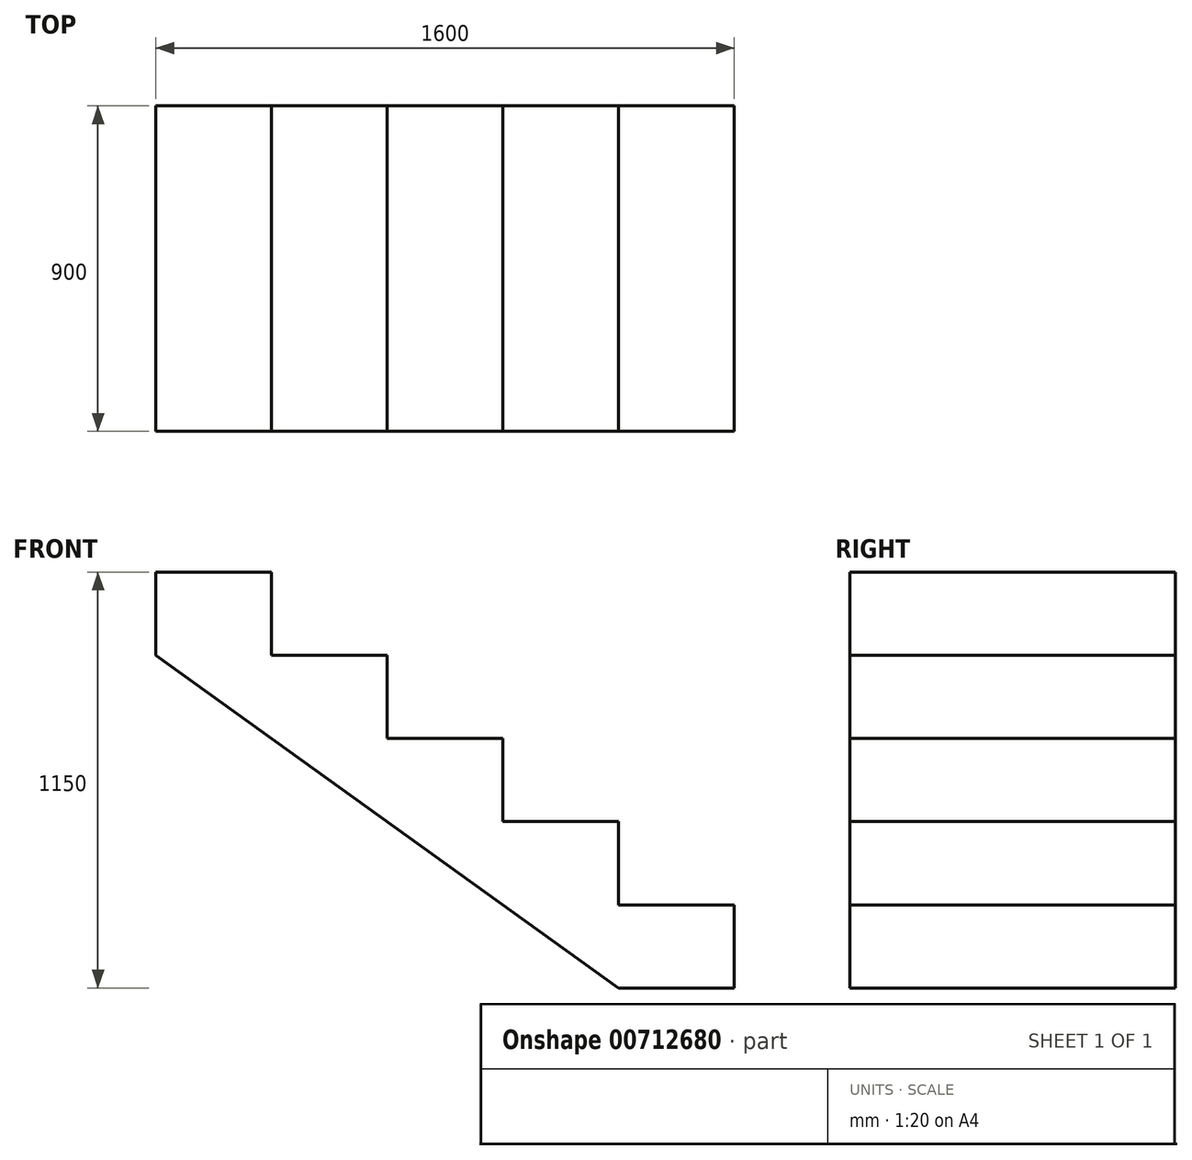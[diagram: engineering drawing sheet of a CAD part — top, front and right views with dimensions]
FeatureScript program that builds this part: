
annotation { "Feature Type Name" : "Feature", "Feature Type Description" : "" }
export const myFeature = defineFeature(function(context is Context, id is Id, definition is map)
    precondition{}
    {
        {
            var Q0;
            Q0=qCreatedBy(makeId("Front.planeOp"),FACE);
            var sketch = newSketch(context, id + "F0", { "sketchPlane" : qUnion([Q0])});
            skLineSegment(sketch, "E0", {"start": v(0, 0) * mm, "end": v(0, 230) * mm});
            skLineSegment(sketch, "E1", {"start": v(0, 230) * mm, "end": v(-320, 230) * mm});
            skLineSegment(sketch, "E2", {"start": v(-320, 230) * mm, "end": v(-320, 460) * mm});
            skLineSegment(sketch, "E3", {"start": v(-320, 460) * mm, "end": v(-640, 460) * mm});
            skLineSegment(sketch, "E4", {"start": v(-640, 460) * mm, "end": v(-640, 690) * mm});
            skLineSegment(sketch, "E5", {"start": v(-640, 690) * mm, "end": v(-960, 690) * mm});
            skLineSegment(sketch, "E6", {"start": v(-960, 690) * mm, "end": v(-960, 920) * mm});
            skLineSegment(sketch, "E7", {"start": v(-960, 920) * mm, "end": v(-1280, 920) * mm});
            skLineSegment(sketch, "E8", {"start": v(-1280, 920) * mm, "end": v(-1280, 1150) * mm});
            skLineSegment(sketch, "E9", {"start": v(-1280, 1150) * mm, "end": v(-1600, 1150) * mm});
            skLineSegment(sketch, "E10", {"start": v(-1600, 1150) * mm, "end": v(-1600, 920) * mm});
            skLineSegment(sketch, "E11", {"start": v(-1600, 920) * mm, "end": v(-320, 0) * mm});
            skLineSegment(sketch, "E12", {"start": v(-320, 0) * mm, "end": v(0, 0) * mm});
            skLineSegment(sketch, "E13", {"start": v(-320, 230) * mm, "end": v(-1280, 920) * mm, "construction": true});
            skSolve(sketch);
        }
        {
            var Q0;
            Q0=makeQuery(id+"F0.imprint","IMPRINT",FACE,{"disambiguationData":[TD([[makeQuery(id+"F0.imprint","IMPRINT",EDGE,{"derivedFrom":sQuery(id+"F0.wireOp",EDGE,"E0")}),1.0]])]});
            extrude(context, id + "F1", {"entities" : qUnion([Q0]), "endBound" : BoundingType.SYMMETRIC, "depth" : 900 * mm, "offsetDistance" : 25 * mm});
        }
    });
